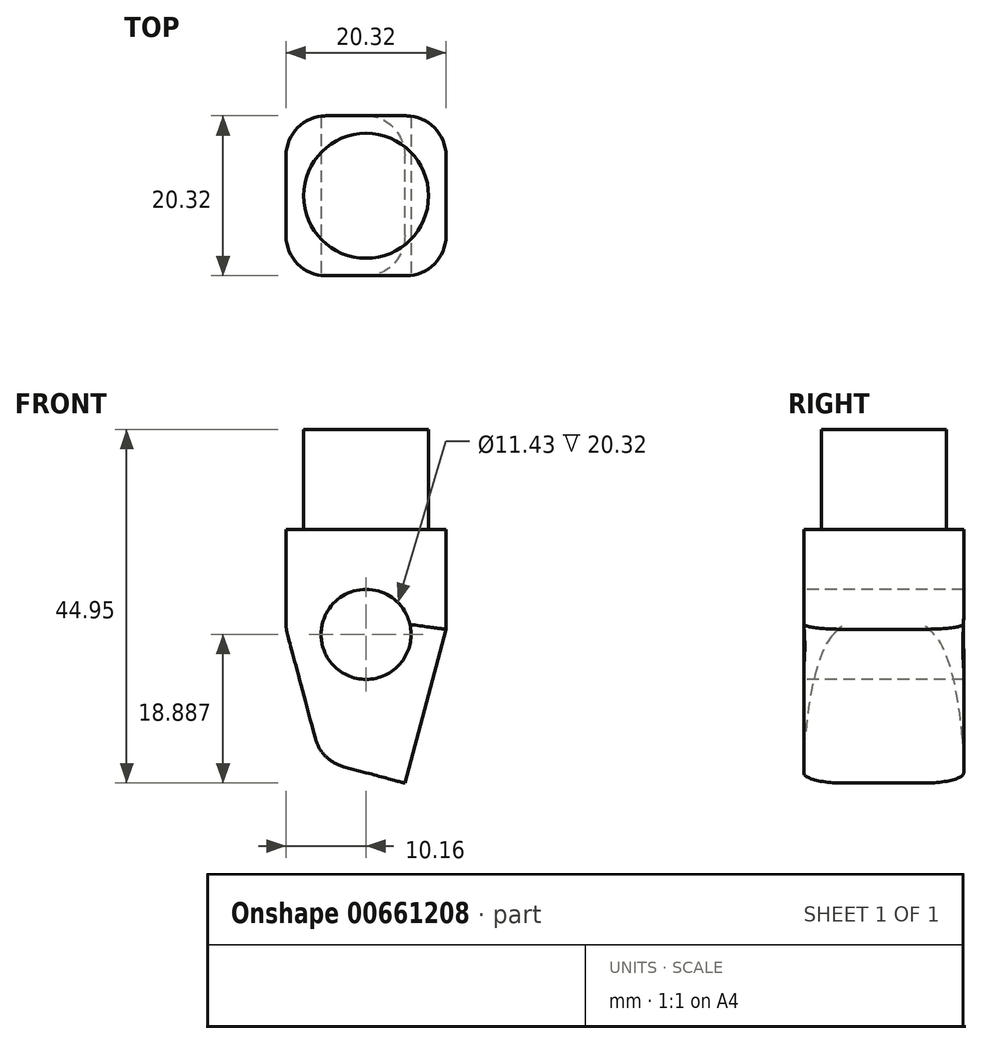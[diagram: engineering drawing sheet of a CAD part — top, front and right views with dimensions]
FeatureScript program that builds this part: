
annotation { "Feature Type Name" : "Feature", "Feature Type Description" : "" }
export const myFeature = defineFeature(function(context is Context, id is Id, definition is map)
    precondition{}
    {
        {
            var Q0;
            Q0=qCreatedBy(makeId("Right.planeOp"),FACE);
            var sketch = newSketch(context, id + "F0", { "sketchPlane" : qUnion([Q0])});
            skLineSegment(sketch, "E0.bottom", {"start": v(-37.98, 14.65) * mm, "end": v(-17.66, 14.65) * mm});
            skLineSegment(sketch, "E0.top", {"start": v(-37.98, -23.45) * mm, "end": v(-17.66, -23.45) * mm});
            skLineSegment(sketch, "E0.left", {"start": v(-37.98, 14.65) * mm, "end": v(-37.98, -23.45) * mm});
            skLineSegment(sketch, "E0.right", {"start": v(-17.66, 14.65) * mm, "end": v(-17.66, -23.45) * mm});
            skSolve(sketch);
        }
        {
            var Q0;
            Q0 = qSketchRegion(id + "F0", true);
            extrude(context, id + "F1", {"entities" : qUnion([Q0]), "depth" : 20.32 * mm, "offsetDistance" : 25.4 * mm});
        }
        {
            var Q0;
            Q0=makeQuery(id+"F1.opExtrude","CAP_EDGE",EDGE,{"disambiguationData":[OSD([sQuery(id+"F0.wireOp",EDGE,"E0.top")])],"isStart":false});
            var Q1;
            Q1=makeQuery(id+"F1.opExtrude","CAP_EDGE",EDGE,{"disambiguationData":[OSD([sQuery(id+"F0.wireOp",EDGE,"E0.top")])],"isStart":true});
            chamfer(context, id + "F2", {"entities" : qUnion([Q0, Q1]), "chamferType" : ChamferType.OFFSET_ANGLE, "width" : 25.4 * mm, "oppositeDirection" : false, "angle" : 15 * degree, "tangentPropagation" : true});
        }
        {
            var Q0;
            Q0=makeQuery(id+"F1.opExtrude","SWEPT_FACE",FACE,{"disambiguationData":[OSD([sQuery(id+"F0.wireOp",EDGE,"E0.left")])]});
            var sketch = newSketch(context, id + "F3", { "sketchPlane" : qUnion([Q0])});
            skCircle(sketch, "E1", {"center": v(10.16, 1.29) * mm, "radius": 5.72 * mm});
            skPoint(sketch, "E1.centerSnap0", {"position": v(10.16, 14.65) * mm});
            skSolve(sketch);
        }
        {
            var Q0;
            Q0 = qSketchRegion(id + "F3", true);
            extrude(context, id + "F4", {"entities" : qUnion([Q0]), "operationType" : NewBodyOperationType.REMOVE, "oppositeDirection" : true, "depth" : 25.4 * mm, "offsetDistance" : 25.4 * mm});
        }
        {
            var Q0;
            {var subQ0=sQuery(id+"F0.wireOp",EDGE,"E0.top");Q0=makeQuery(id+"F2.opChamfer","BLEND_FACE",FACE,{"disambiguationData":[OSD([subQ0]),TDD([makeQuery(id+"F1.opExtrude","CAP_EDGE",EDGE,{"disambiguationData":[OSD([subQ0])],"isStart":false})])]});}
            var sketch = newSketch(context, id + "F5", { "sketchPlane" : qUnion([Q0])});
            skLineSegment(sketch, "E2.bottom", {"start": v(-57.9, -13.1) * mm, "end": v(10.68, -13.1) * mm});
            skLineSegment(sketch, "E2.top", {"start": v(-57.9, -23.68) * mm, "end": v(10.68, -23.68) * mm});
            skLineSegment(sketch, "E2.left", {"start": v(-57.9, -13.1) * mm, "end": v(-57.9, -23.68) * mm});
            skLineSegment(sketch, "E2.right", {"start": v(10.68, -13.1) * mm, "end": v(10.68, -23.68) * mm});
            skSolve(sketch);
        }
        {
            var Q0;
            Q0 = qSketchRegion(id + "F5", true);
            extrude(context, id + "F6", {"entities" : qUnion([Q0]), "operationType" : NewBodyOperationType.REMOVE, "oppositeDirection" : true, "depth" : 35.56 * mm, "offsetDistance" : 25.4 * mm});
        }
        {
            var Q0;
            Q0=makeQuery(id+"F1.opExtrude","SWEPT_FACE",FACE,{"disambiguationData":[OSD([sQuery(id+"F0.wireOp",EDGE,"E0.bottom")])]});
            var sketch = newSketch(context, id + "F7", { "sketchPlane" : qUnion([Q0])});
            skCircle(sketch, "E3", {"center": v(10.16, -27.82) * mm, "radius": 7.94 * mm});
            skPoint(sketch, "E3.centerSnap0", {"position": v(0, -27.82) * mm});
            skPoint(sketch, "E3.centerSnap1", {"position": v(10.16, -37.98) * mm});
            skSolve(sketch);
        }
        {
            var Q0;
            Q0 = qSketchRegion(id + "F7", true);
            extrude(context, id + "F8", {"entities" : qUnion([Q0]), "operationType" : NewBodyOperationType.ADD, "depth" : 12.7 * mm, "offsetDistance" : 25.4 * mm});
        }
        {
            var Q0;
            Q0=makeQuery(id+"F1.opExtrude","CAP_EDGE",EDGE,{"disambiguationData":[OSD([sQuery(id+"F0.wireOp",EDGE,"E0.right")])],"isStart":false});
            var Q1;
            Q1=makeQuery(id+"F1.opExtrude","CAP_EDGE",EDGE,{"disambiguationData":[OSD([sQuery(id+"F0.wireOp",EDGE,"E0.right")])],"isStart":true});
            var Q2;
            Q2=makeQuery(id+"F1.opExtrude","CAP_EDGE",EDGE,{"disambiguationData":[OSD([sQuery(id+"F0.wireOp",EDGE,"E0.left")])],"isStart":true});
            var Q3;
            Q3=makeQuery(id+"F1.opExtrude","CAP_EDGE",EDGE,{"disambiguationData":[OSD([sQuery(id+"F0.wireOp",EDGE,"E0.left")])],"isStart":false});
            var Q4;
            Q4=makeQuery(id+"F2.opChamfer","BLEND_EDGE",EDGE,{"blendedFrom":[makeQuery(id+"F1.opExtrude","CAP_EDGE",EDGE,{"disambiguationData":[OSD([sQuery(id+"F0.wireOp",EDGE,"E0.top")])],"isStart":false}),makeQuery(id+"F1.opExtrude","SWEPT_FACE",FACE,{"disambiguationData":[OSD([sQuery(id+"F0.wireOp",EDGE,"E0.left")])]})],"blendedInto":[makeQuery(id+"F1.opExtrude","SWEPT_FACE",FACE,{"disambiguationData":[OSD([sQuery(id+"F0.wireOp",EDGE,"E0.left")])]})]});
            var Q5;
            Q5=makeQuery(id+"F2.opChamfer","BLEND_EDGE",EDGE,{"blendedFrom":[makeQuery(id+"F1.opExtrude","CAP_EDGE",EDGE,{"disambiguationData":[OSD([sQuery(id+"F0.wireOp",EDGE,"E0.top")])],"isStart":false}),makeQuery(id+"F1.opExtrude","SWEPT_FACE",FACE,{"disambiguationData":[OSD([sQuery(id+"F0.wireOp",EDGE,"E0.right")])]})],"blendedInto":[makeQuery(id+"F1.opExtrude","SWEPT_FACE",FACE,{"disambiguationData":[OSD([sQuery(id+"F0.wireOp",EDGE,"E0.right")])]})]});
            var Q6;
            {var subQ0=sQuery(id+"F0.wireOp",EDGE,"E0.top");Q6=makeQuery(id+"F6.boolean.opBoolean","INTERSECT",EDGE,{"derivedFrom":[makeQuery(id+"F2.opChamfer","BLEND_FACE",FACE,{"disambiguationData":[OSD([subQ0]),TDD([makeQuery(id+"F1.opExtrude","CAP_EDGE",EDGE,{"disambiguationData":[OSD([subQ0])],"isStart":true})])]}),makeQuery(id+"F6.opExtrude","SWEPT_FACE",FACE,{"disambiguationData":[OSD([sQuery(id+"F5.wireOp",EDGE,"E2.bottom")])]})]});}
            var Q7;
            {var subQ0=sQuery(id+"F0.wireOp",EDGE,"E0.top");Q7=makeQuery(id+"F2.opChamfer","BLEND_EDGE",EDGE,{"blendedFrom":[makeQuery(id+"F1.opExtrude","CAP_EDGE",EDGE,{"disambiguationData":[OSD([subQ0])],"isStart":true}),makeQuery(id+"F1.opExtrude","CAP_FACE",FACE,{"disambiguationData":[OSD([sQuery(id+"F0.wireOp",EDGE,"E0.bottom"),subQ0,sQuery(id+"F0.wireOp",EDGE,"E0.left"),sQuery(id+"F0.wireOp",EDGE,"E0.right")])],"isStart":true})],"blendedInto":[makeQuery(id+"F1.opExtrude","CAP_FACE",FACE,{"disambiguationData":[OSD([sQuery(id+"F0.wireOp",EDGE,"E0.bottom"),subQ0,sQuery(id+"F0.wireOp",EDGE,"E0.left"),sQuery(id+"F0.wireOp",EDGE,"E0.right")])],"isStart":true})]});}
            fillet(context, id + "F9", {"entities" : qUnion([Q0, Q1, Q2, Q3, Q4, Q5, Q6, Q7]), "radius" : 5.08 * mm, "tangentPropagation" : true, "allowEdgeOverflow" : false});
        }
    });
